# Revit family: 2021_ES_Puerta_Ferroflex-RapidaEnrollable_Fenroll_D00683ES
name_source: partatom
category: Doors
units: mm (PartAtom-declared; Revit-internal decimal feet)

## family parameters
Always vertical = Yes
Cut with Voids When Loaded = No
Host = Wall
OmniClass Number = 23.30.10.00
OmniClass Title = Doors
Room Calculation Point = No
Shared = No

## types (1)
- Puerta enrollable 4500 x 4500 m
    A = 240 mm  [stored 0.787402 ft]
    Acabado = Lacado
    Acidificacion Atmosferica por Unidad = 0
    Agua Consumida por Unidad = 0
    Altura cuadro de Mando = 1200 mm
    Altura minima requerida = 2100 mm
    Altura útil = 4500 mm
    Analytic Construction = <Ninguno>
    Ancho útil = 4500 mm
    Antepecho Externo = No
    Antepecho Interno = No
    Area Acristalamiento = Posibilidad de Mirillas
    Area de superficie = 0 m²
    Autor = Bimetica Parametric Design Services S.L.
    B = 240 mm  [stored 0.787402 ft]
    C = 500 mm  [stored 1.64042 ft]
    COBie Categoria = IfcDoor
    Cambio Climatico por Unidad = 0
    Cierre automatico = No
    Clasificacion de carga de viento = Clase 2
    Clasificacion de seguridad = ISO 1421 / ISO 13937-2
    Codigo = Fenroll
    Contenido Garantia = Materiales
    Cortahumos = No
    Coste Mantenimiento = 0
    D = 115 mm  [stored 0.377297 ft]
    Define Thermal Properties by = Schematic Type
    Description = Puerta rápida enrollable, compuesta por guías y cabezal en acero lacado o inoxidable. Lona de PVC con tejido de poliéster, color a elegir. Cuadro de maniobra con variador. Seguridad activa mediante barreras de fotocélulas cruzadas y posibilidad de faldón inferior con banda resistiva.
    Desfae Interior = 0 mm  [stored 0 ft]
    Desfase Exterior = 0 mm  [stored 0 ft]
    Destruccion Capa Ozono Estratosferica por Unidad = 0
    E = 110 mm  [stored 0.360892 ft]
    Energia No Renovable Consumida por Unidad = 0
    Energia Primaria Total Consumida por Unidad = 0
    Energia Renovable Consumida por Unidad = 0
    Energia consumida = 0
    Es Accesible = No
    Es Exterior = Yes
    Es Motorizada = Yes
    Espacio libre acceso = 0 mm  [stored 0 ft]
    Estandar seguridad = 2006/42/CE
    Etiqueta Modelo = Puerta enrollable modelo Fenroll
    Eutrofizacion por Unidad = 0
    Falta de Recursos por Unidad = 0
    Fecha Emision Elemento BIM = 29/11/2022
    Fecha Vencimiento Elemento BIM = 2 años vista
    Fire Rating = Lona ISO 3795-89
    Formacion Fotoquimica Ozono por Unidad = 0
    Fraccion del area de acristalamiento = 0
    Frame Projection Ext. = 25 mm  [stored 0.082021 ft]
    Frame Projection Int. = 25 mm  [stored 0.082021 ft]
    Function = Interior
    G = 320 mm  [stored 1.04987 ft]
    Garantia Extendida = No
    Gubimclass Codigo = 80.10.40.20
    Gubimclass Titulo = Puertas de acceso
    Height = 4500 mm
    Historial = (RVT2021) Creación de Elemento.
    IfcExportAs = IfcDoor
    IfcExportType = Roll-up door
    Infiltracion = 0
    Lugar Ensamblaje = En obra
    Manufacturer = Ferroflex S.L.U.
    Marcado CE = Yes
    Masterformat Codigo = 08 31 00
    Masterformat Titulo = Access Doors and Panels
    Material = Hierro_Lacado
    Material Contenedor = Caja de madera
    Material Envoltura = Envoltura de plástico
    Material Telon = PVC_Azul
    Model = Fenroll
    Numero Articulo = D00683ES-V2
    Numero de Licencia = XXX-XXXX7125
    Omniclass Codigo = 23-17 11 27 13
    Omniclass Titulo = Access Doors
    Operation = Enrrollable
    Periodo Garantia = 1 año vista
    Peso = 0.00 kg
    Plataforma descaga contenido BIM = www.bimetica.com
    Referencia = D00683ES-V2
    Residuo Inerte por Unidad = 0
    Residuo Radioactivo por Unidad = 0
    Residuos No Peligrosos por Unidad = 0
    Residuos Peligrosos por Unidad = 0
    Salida Humos = No
    Salida de incendios = No
    Serie = Puertas enrrollables
    Soporte tecnico BIM = https://bimsupport.info
    Thickness = 20 mm  [stored 0.0656168 ft]
    Titular = MANUSA GEST, S.L.
    UNSPSC Codigo = 30171503
    UNSPSC Titulo = Rolling doors
    URL = https://ferroflexindustrialaccess.com
    URL Perfil BIM = https://bimetica.com
    URL Producto = https://ferroflexindustrialaccess.com
    URL de Declaracion de Prestaciones = https://ferroflexindustrialaccess.com
    Unidad Medicion = Unidad
    Version = RVT2021
    Version Estandar GDO-BIM = GDO-BIM V02
    Wall Closure = Interior
    Width = 4500 mm

note: [stored X ft] marks values corroborated as IEEE doubles in the binary element streams (Revit-internal decimal feet)

## geometry (parser evidence)
native form markers: Sweep x2
no freeform markers — native parametric forms only
